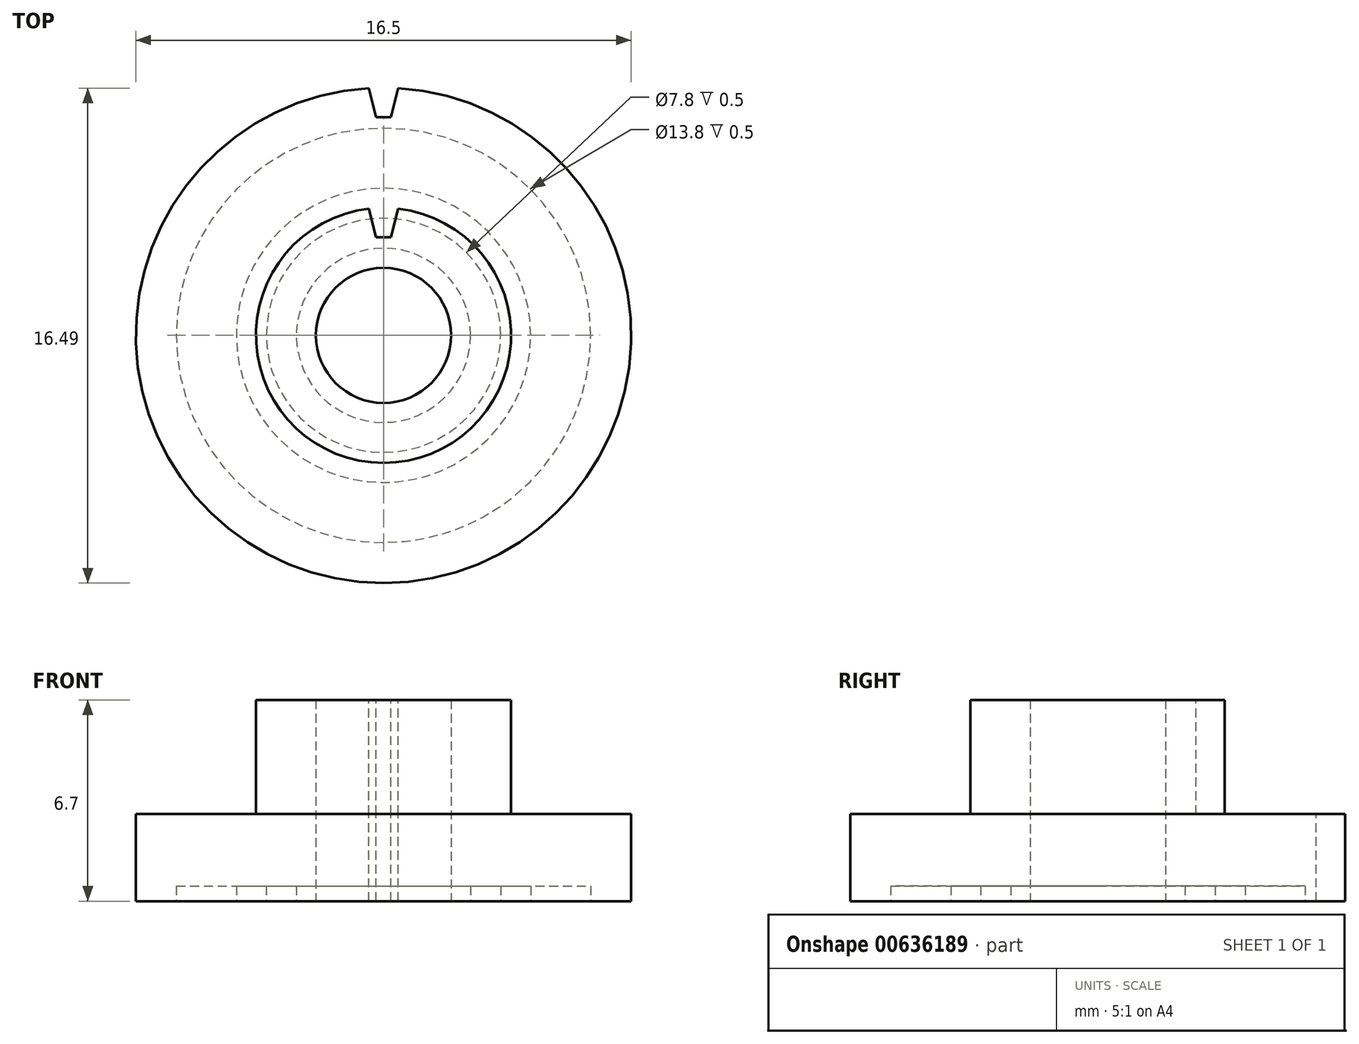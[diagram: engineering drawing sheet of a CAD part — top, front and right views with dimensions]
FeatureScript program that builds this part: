
annotation { "Feature Type Name" : "Feature", "Feature Type Description" : "" }
export const myFeature = defineFeature(function(context is Context, id is Id, definition is map)
    precondition{}
    {
        {
            var Q0;
            Q0=qCreatedBy(makeId("Top.planeOp"),FACE);
            var sketch = newSketch(context, id + "F0", { "sketchPlane" : qUnion([Q0])});
            skCircle(sketch, "E0", {"center": v(0, 0) * mm, "radius": 8.25 * mm});
            skSolve(sketch);
        }
        {
            var Q0;
            Q0=makeQuery(id+"F0.imprint","IMPRINT",FACE,{"disambiguationData":[TD([[makeQuery(id+"F0.imprint","IMPRINT",EDGE,{"derivedFrom":sQuery(id+"F0.wireOp",EDGE,"E0")}),1.0]])]});
            extrude(context, id + "F1", {"entities" : qUnion([Q0]), "depth" : 2.9 * mm});
        }
        {
            var Q0;
            Q0=makeQuery(id+"F1.opExtrude","CAP_FACE",FACE,{"disambiguationData":[OSD([sQuery(id+"F0.wireOp",EDGE,"E0")])],"isStart":false});
            var sketch = newSketch(context, id + "F2", { "sketchPlane" : qUnion([Q0])});
            skCircle(sketch, "E1", {"center": v(0, 0) * mm, "radius": 4.25 * mm});
            skSolve(sketch);
        }
        {
            var Q0;
            Q0=makeQuery(id+"F2.imprint","IMPRINT",FACE,{"disambiguationData":[TD([[makeQuery(id+"F2.imprint","IMPRINT",EDGE,{"derivedFrom":sQuery(id+"F2.wireOp",EDGE,"E1")}),1.0]])]});
            extrude(context, id + "F3", {"entities" : qUnion([Q0]), "operationType" : NewBodyOperationType.ADD, "depth" : 3.8 * mm});
        }
        {
            var Q0;
            Q0=makeQuery(id+"F1.opExtrude","CAP_FACE",FACE,{"disambiguationData":[OSD([sQuery(id+"F0.wireOp",EDGE,"E0")])],"isStart":false});
            var sketch = newSketch(context, id + "F4", { "sketchPlane" : qUnion([Q0])});
            skCircle(sketch, "E2", {"center": v(0, 0) * mm, "radius": 7.27 * mm, "construction": true});
            skLineSegment(sketch, "E3", {"start": v(3.7, 6.26) * mm, "end": v(4.37, 7) * mm, "construction": true});
            skLineSegment(sketch, "E4", {"start": v(-0.5, 8.24) * mm, "end": v(-0.25, 7.27) * mm});
            skLineSegment(sketch, "E5", {"start": v(-0.25, 7.27) * mm, "end": v(0.25, 7.27) * mm});
            skLineSegment(sketch, "E6", {"start": v(0.25, 7.27) * mm, "end": v(0.5, 8.24) * mm});
            skSolve(sketch);
        }
        {
            var Q0;
            {var subQ0=sQuery(id+"F4.wireOp",EDGE,"E4");Q0=makeQuery(id+"F4.imprint","IMPRINT",FACE,{"disambiguationData":[TD([[makeQuery(id+"F4.imprint","IMPRINT",EDGE,{"derivedFrom":subQ0}),1.0]])]});}
            extrude(context, id + "F5", {"entities" : qUnion([Q0]), "operationType" : NewBodyOperationType.REMOVE, "oppositeDirection" : true, "depth" : 2.9 * mm});
        }
        {
            var Q0;
            Q0=makeQuery(id+"F3.opExtrude","CAP_FACE",FACE,{"disambiguationData":[OSD([sQuery(id+"F2.wireOp",EDGE,"E1")])],"isStart":false});
            var sketch = newSketch(context, id + "F6", { "sketchPlane" : qUnion([Q0])});
            skCircle(sketch, "E7", {"center": v(0, 0) * mm, "radius": 3.28 * mm, "construction": true});
            skLineSegment(sketch, "E8", {"start": v(1.84, 2.71) * mm, "end": v(2.6, 3.36) * mm, "construction": true});
            skLineSegment(sketch, "E9", {"start": v(-0.49, 4.22) * mm, "end": v(-0.25, 3.27) * mm});
            skLineSegment(sketch, "E10", {"start": v(-0.25, 3.27) * mm, "end": v(0.25, 3.27) * mm});
            skLineSegment(sketch, "E11", {"start": v(0.25, 3.27) * mm, "end": v(0.49, 4.22) * mm});
            skSolve(sketch);
        }
        {
            var Q0;
            {var subQ0=sQuery(id+"F6.wireOp",EDGE,"E9");Q0=makeQuery(id+"F6.imprint","IMPRINT",FACE,{"disambiguationData":[TD([[makeQuery(id+"F6.imprint","IMPRINT",EDGE,{"derivedFrom":subQ0}),1.0]])]});}
            extrude(context, id + "F7", {"entities" : qUnion([Q0]), "operationType" : NewBodyOperationType.REMOVE, "oppositeDirection" : true, "depth" : 3.8 * mm});
        }
        {
            var Q0;
            Q0=makeQuery(id+"F1.opExtrude","CAP_FACE",FACE,{"disambiguationData":[OSD([sQuery(id+"F0.wireOp",EDGE,"E0")])],"isStart":true});
            var sketch = newSketch(context, id + "F8", { "sketchPlane" : qUnion([Q0])});
            skCircle(sketch, "E12", {"center": v(0, 0) * mm, "radius": 2.25 * mm});
            skCircle(sketch, "E13", {"center": v(0, 0) * mm, "radius": 6.9 * mm});
            skCircle(sketch, "E14", {"center": v(0, 0) * mm, "radius": 4.9 * mm});
            skLineSegment(sketch, "E15", {"start": v(0, -4.9) * mm, "end": v(0, -6.9) * mm, "construction": true});
            skCircle(sketch, "E16", {"center": v(0, 0) * mm, "radius": 2.9 * mm});
            skLineSegment(sketch, "E17", {"start": v(0, -2.9) * mm, "end": v(0, -4.9) * mm, "construction": true});
            skCircle(sketch, "E18", {"center": v(0, 0) * mm, "radius": 3.9 * mm});
            skLineSegment(sketch, "E19", {"start": v(0, 2.9) * mm, "end": v(0, 3.9) * mm, "construction": true});
            skSolve(sketch);
        }
        {
            var Q0;
            Q0=makeQuery(id+"F8.imprint","IMPRINT",FACE,{"disambiguationData":[TD([[makeQuery(id+"F8.imprint","IMPRINT",EDGE,{"derivedFrom":sQuery(id+"F8.wireOp",EDGE,"E12")}),1.0]])]});
            extrude(context, id + "F9", {"entities" : qUnion([Q0]), "operationType" : NewBodyOperationType.REMOVE, "oppositeDirection" : true, "depth" : 6.7 * mm});
        }
        {
            var Q0;
            Q0=makeQuery(id+"F8.imprint","IMPRINT",FACE,{"disambiguationData":[TD([[makeQuery(id+"F8.imprint","IMPRINT",EDGE,{"derivedFrom":sQuery(id+"F8.wireOp",EDGE,"E16")}),-1.0]])]});
            var Q1;
            Q1=makeQuery(id+"F8.imprint","IMPRINT",FACE,{"disambiguationData":[TD([[makeQuery(id+"F8.imprint","IMPRINT",EDGE,{"derivedFrom":sQuery(id+"F8.wireOp",EDGE,"E13")}),1.0]])]});
            extrude(context, id + "F10", {"entities" : qUnion([Q0, Q1]), "operationType" : NewBodyOperationType.REMOVE, "oppositeDirection" : true, "depth" : 0.5 * mm});
        }
    });
